# Revit family: 3079315 Lighting Fixture_Sylvania_Instar Eco Kit LED Fixed SunDim_Ceiling Recessed
name_source: partatom
category: Lighting Fixtures
revit_build: Autodesk Revit 2017 (Build: 20190507_1515(x64)
units: mm (PartAtom-declared; Revit-internal decimal feet)

## family parameters
Cut with Voids When Loaded = No
Host = Face
Light Source = Yes
OmniClass Number = 23.80.70.11.17
OmniClass Title = Specialized Lighting by Location or Use
Part Type = Normal
Room Calculation Point = No
Round Connector Dimension = Use Diameter
Shared = No

## types (1)
- Instar Eco Kit LED WH FIX HD
    Accessory Material = Aluminum_Sylvania_Instar Eco Kit LED Fixed SunDim_White
    Apparent Load = 12 VA
    Assembly Code = D5020200
    Beam Angle = 36°
    Body Material = Steel_Sylvania_Instar Eco Kit LED Fixed SunDim_Silver
    CRI (Ra) = 92-94
    Catalog Number = 3079315 Instar Eco Kit LED WH FIX HD
    Color Filter = 16777215
    Cutout Diameter = 68 mm  [stored 0.223097 ft]
    Default Elevation = 0 mm  [stored 0 ft]
    Description = Significant energy savings compared to traditional CFL and 2D fixtures . Excellent flashing provides perfect homogenous light distribution . Unique feature allowing a choice between High Output or High efficiency with the flick of a switch. 50,000 hours life, providing a maintenance free lighting solution . Halo backlight . IP65 fitting resistant to dust and water jet ingress. Tamper resistant locking feature . Ceiling or wall mounted . Integral emergency options suitable for use on defined escape routes. Low profile fitting . Choice of White and Brushed Aluminium trim finishes. Option to add microwave sensor for maximum energy savings
    Diameter = 78 mm  [stored 0.255906 ft]
    Diffuser Diameter = 32 mm  [stored 0.104987 ft]
    Diffuser Material = Polycarbonate_Sylvania_Instar Eco Kit LED Fixed SunDimi_Clear
    Dimming Lamp Color Temperature Shift = <None>
    Drive Current = 350mA
    Emit Shape Visible in Rendering = No
    Emit from Circle Diameter = 32 mm  [stored 0.104987 ft]
    Energy Class = A++, A+, A
    Height = 50 mm  [stored 0.164042 ft]
    Housing Radius = 31 mm  [stored 0.101706 ft]
    IP Rating = IP44
    Lamp = LED
    Lamp Comments = Integrated LED
    Life = 35 000 h
    Manufacturer = Feilo Sylvania
    Model = Instar Eco Kit LED WH FIX HD
    Photometric Web File = 3079315_InstarEcoKitLEDWHFIXHD-191613.ies
    Product Family = Instar Eco Kit LED Fixed SunDim
    Product Page URL = http://www.sylvania-lighting.com
    Radius = 39 mm  [stored 0.127953 ft]
    Reflector Diameter = 38 mm  [stored 0.124672 ft]
    Reflector Material = Steel_Sylvania_Instar Eco Kit LED Fixed SunDim_Silver
    Reflector Radius = 19 mm  [stored 0.062336 ft]
    Tilt Angle = -90°
    URL = http://www.sylvania-lighting.com
    Voltage = 230 V
    Voltage Comments = UNV (Universal Voltage; 220-240 Volt)

note: [stored X ft] marks values corroborated as IEEE doubles in the binary element streams (Revit-internal decimal feet)

## geometry (parser evidence)
native form markers: Blend x6, Sweep x1
no freeform markers — native parametric forms only
